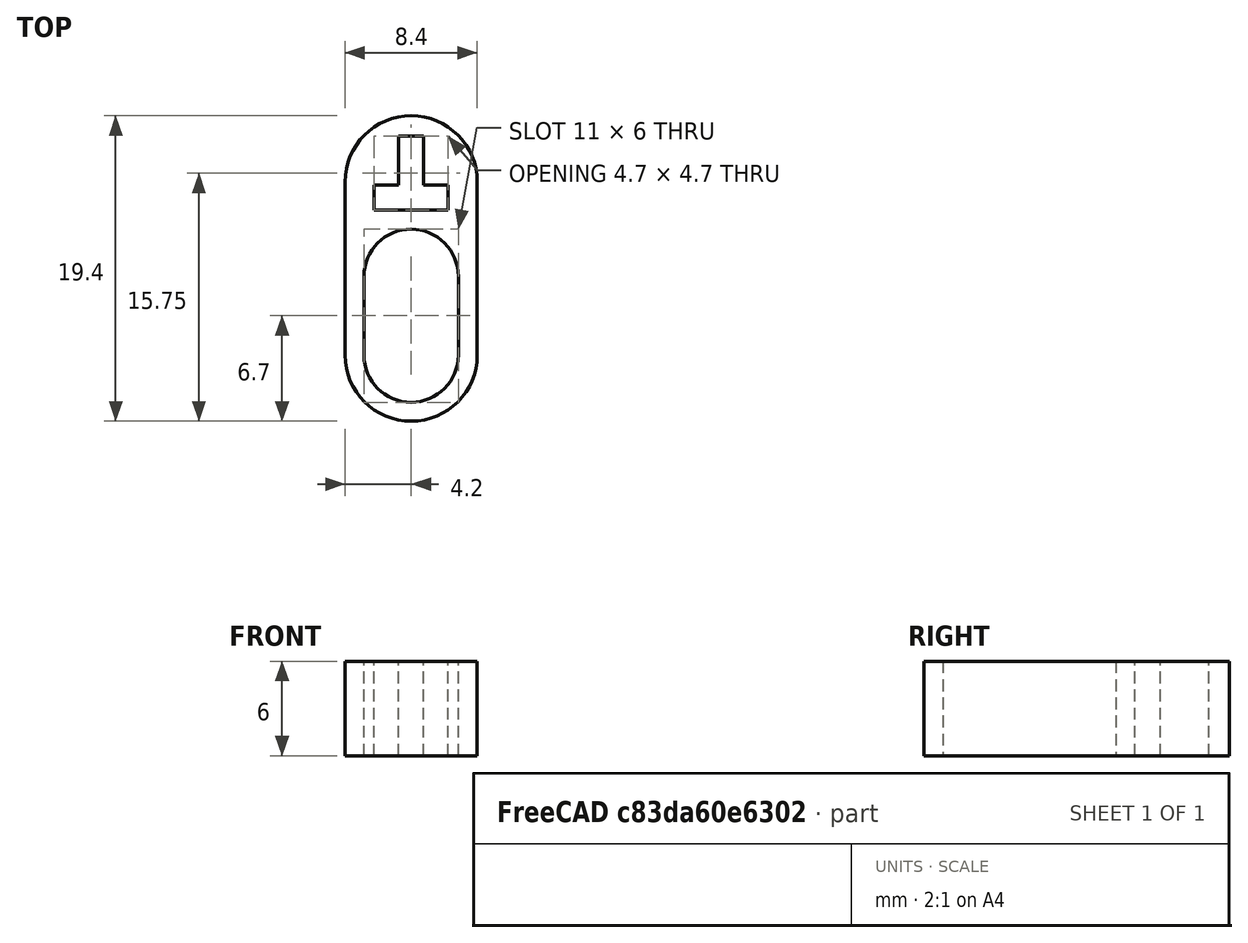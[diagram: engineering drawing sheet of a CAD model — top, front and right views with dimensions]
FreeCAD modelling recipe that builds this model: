
FCSTD DOCUMENT  (FreeCAD 0.20R29177 +426 (Git))
Label: SensorWireClip
License: All rights reserved
LicenseURL: http://en.wikipedia.org/wiki/All_rights_reserved
objects: Sketcher::SketchObject×1, PartDesign::Pad×1, PartDesign::Body×1
note: 4 computed .brp shape members not serialized (recipe doc carries the construction recipe); baked Part::Feature solids carry a one-line shape summary decoded from their .brp

FEATURE [Sketcher::SketchObject] Sketch
  FullyConstrained = true
  MapMode = 5
  Support = -> [XY_Plane]
  sketch-geometry (20):
    g0: LineSegment StartX=-2.35 StartY=0 StartZ=0 EndX=-2.35 EndY=-1.6 EndZ=0
    g1: LineSegment StartX=-2.35 StartY=-1.6 StartZ=0 EndX=2.35 EndY=-1.6 EndZ=0
    g2: LineSegment StartX=2.35 StartY=-1.6 StartZ=0 EndX=2.35 EndY=0 EndZ=0
    g3: GeomPoint X=0 Y=-0.8 Z=0
    g4: LineSegment StartX=-0.8 StartY=3.1 StartZ=0 EndX=-0.8 EndY=0 EndZ=0
    g5: LineSegment StartX=-0.8 StartY=0 StartZ=0 EndX=0.8 EndY=0 EndZ=0
    g6: LineSegment StartX=0.8 StartY=0 StartZ=0 EndX=0.8 EndY=3.1 EndZ=0
    g7: LineSegment StartX=0.8 StartY=3.1 StartZ=0 EndX=-0.8 EndY=3.1 EndZ=0
    g8: GeomPoint X=0 Y=1.55 Z=0
    g9: LineSegment StartX=2.35 StartY=0 StartZ=0 EndX=0.8 EndY=0 EndZ=0
    g10: LineSegment StartX=-0.8 StartY=0 StartZ=0 EndX=-2.35 EndY=0 EndZ=0
    g11: ArcOfCircle CenterX=0 CenterY=-5.8 CenterZ=0 NormalX=0 NormalY=0 NormalZ=1 AngleXU=0 Radius=3 StartAngle=0 EndAngle=3.14159
    g12: ArcOfCircle CenterX=0 CenterY=-10.8 CenterZ=0 NormalX=0 NormalY=0 NormalZ=1 AngleXU=0 Radius=3 StartAngle=3.14159 EndAngle=6.28319
    g13: LineSegment StartX=-3 StartY=-5.8 StartZ=0 EndX=-3 EndY=-10.8 EndZ=0
    g14: LineSegment StartX=3 StartY=-10.8 StartZ=0 EndX=3 EndY=-5.8 EndZ=0
    g15: ArcOfCircle CenterX=0 CenterY=-10.8 CenterZ=0 NormalX=0 NormalY=0 NormalZ=1 AngleXU=0 Radius=4.2 StartAngle=3.14159 EndAngle=6.28319
    g16: ArcOfCircle CenterX=0 CenterY=0.2 CenterZ=0 NormalX=0 NormalY=0 NormalZ=1 AngleXU=0 Radius=4.2 StartAngle=0 EndAngle=3.14159
    g17: LineSegment StartX=4.2 StartY=-10.8 StartZ=0 EndX=4.2 EndY=0.2 EndZ=0
    g18: LineSegment StartX=-4.2 StartY=0.2 StartZ=0 EndX=-4.2 EndY=-10.8 EndZ=0
    g19: LineSegment StartX=0 StartY=-1.6 StartZ=0 EndX=0 EndY=-2.8 EndZ=0
  constraints (51):
    c: Coincident(g0,g1)
    c: Coincident(g1,g2)
    c: Coincident(g2,g9)
    c: Coincident(g10,g0)
    c: Horizontal(g1)
    c: Vertical(g0)
    c: Vertical(g2)
    c: Symmetric(g1,g0,g3)
    c: PointOnObject(g3,g-2)
    c: Coincident(g4,g5)
    c: Coincident(g5,g6)
    c: Coincident(g6,g7)
    c: Coincident(g7,g4)
    c: Horizontal(g5)
    c: Horizontal(g7)
    c: Vertical(g4)
    c: Vertical(g6)
    c: Symmetric(g5,g4,g8)
    c: PointOnObject(g8,g-2)
    c: Horizontal(g9)
    c: Horizontal(g10)
    c: Coincident(g9,g5)
    c: Coincident(g4,g10)
    c: PointOnObject(g2,g-1)
    c: DistanceY(g2,g2) = 1.6
    c: Equal(g7,g2)
    c: DistanceX(g1,g1) = 4.7
    c: DistanceY(g0,g4) = 4.7
    c: Tangent(g11,g13) = -1.5708
    c: Tangent(g13,g12) = -1.5708
    c: Tangent(g12,g14) = -1.5708
    c: Tangent(g14,g11) = -1.5708
    c: Equal(g11,g12)
    c: PointOnObject(g11,g-2)
    c: PointOnObject(g12,g-2)
    c: Diameter(g11) = 6
    c: Tangent(g15,g17) = -1.5708
    c: Tangent(g17,g16) = -1.5708
    c: Tangent(g16,g18) = -1.5708
    c: Tangent(g18,g15) = -1.5708
    c: Equal(g15,g16)
    c: Coincident(g15,g12)
    c: PointOnObject(g16,g-2)
    c: DistanceY(g12,g11) = 5
    c: DistanceY(g-1,g16) = 0.2
    c: PointOnObject(g19,g1)
    c: PointOnObject(g19,g11)
    c: Vertical(g19)
    c: PointOnObject(g19,g-2)
    c: DistanceY(g19,g19) = 1.2
    c: DistanceX(g12,g15) = 1.2
FEATURE [PartDesign::Pad] Pad
  Direction = (0,0,1)
  Length = 6
  Length2 = 10
  Profile = -> Sketch
  ReferenceAxis = -> Sketch [N_Axis]
  Type = 0
FEATURE [PartDesign::Body] Body
  Group = -> [Sketch,Pad]
  Origin = -> Origin
  Tip = -> Pad
